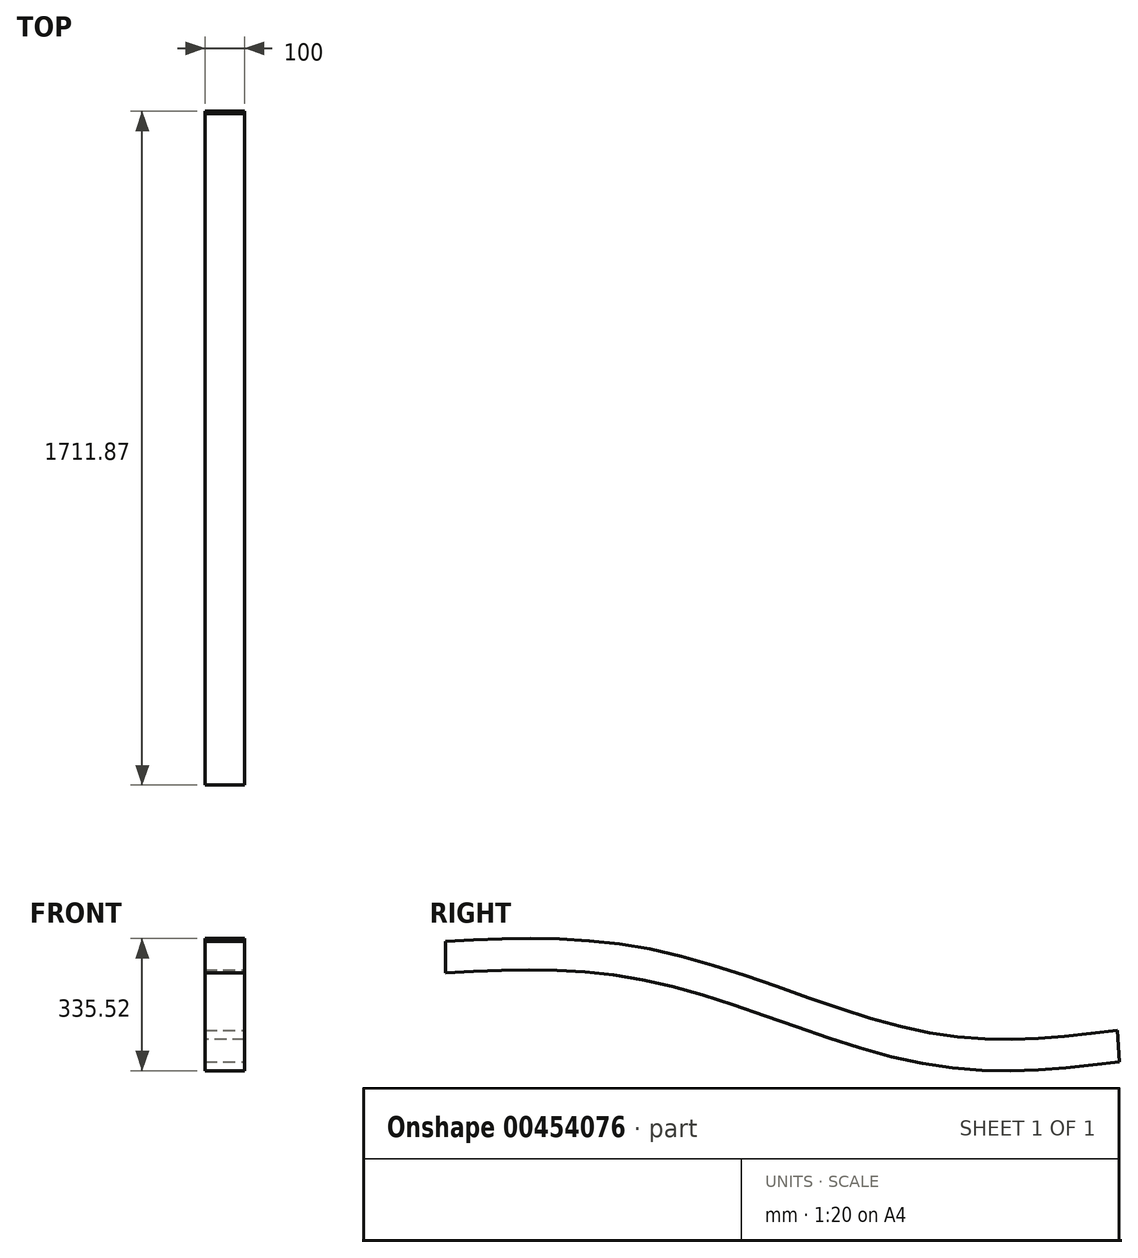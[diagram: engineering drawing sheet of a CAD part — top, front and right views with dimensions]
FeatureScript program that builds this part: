
annotation { "Feature Type Name" : "Feature", "Feature Type Description" : "" }
export const myFeature = defineFeature(function(context is Context, id is Id, definition is map)
    precondition{}
    {
        {
            var Q0;
            Q0=qCreatedBy(makeId("Front.planeOp"),FACE);
            var sketch = newSketch(context, id + "F0", { "sketchPlane" : qUnion([Q0])});
            skLineSegment(sketch, "E0.bottom", {"start": v(-50, 40) * mm, "end": v(50, 40) * mm});
            skLineSegment(sketch, "E0.top", {"start": v(-50, -40) * mm, "end": v(50, -40) * mm});
            skLineSegment(sketch, "E0.left", {"start": v(-50, 40) * mm, "end": v(-50, -40) * mm});
            skLineSegment(sketch, "E0.right", {"start": v(50, 40) * mm, "end": v(50, -40) * mm});
            skPoint(sketch, "E0.middle", {"position": v(0, 0) * mm});
            skSolve(sketch);
        }
        {
            var Q0;
            Q0=qCreatedBy(makeId("Right.planeOp"),FACE);
            var sketch = newSketch(context, id + "F1", { "sketchPlane" : qUnion([Q0])});
            skFitSpline(sketch, "E1", {"points": [v(0, 0) * mm, v(544.63, -25.77) * mm, v(1210.8, -229.44) * mm, v(1709.18, -226.44) * mm], "startDerivative": vector(1631.64, 79.72) * mm, "endDerivative": vector(1547.98, 180.59) * mm});
            skSolve(sketch);
        }
        {
            var Q0;
            Q0=makeQuery(id+"F0.imprint","IMPRINT",FACE,{"disambiguationData":[TD([[makeQuery(id+"F0.imprint","IMPRINT",EDGE,{"derivedFrom":sQuery(id+"F0.wireOp",EDGE,"E0.bottom")}),-1.0]])]});
            var Q1;
            Q1=sQuery(id+"F1.wireOp",EDGE,"E1");
            sweep(context, id + "F2", {"profiles" : qUnion([Q0]), "path" : qUnion([Q1])});
        }
    });
